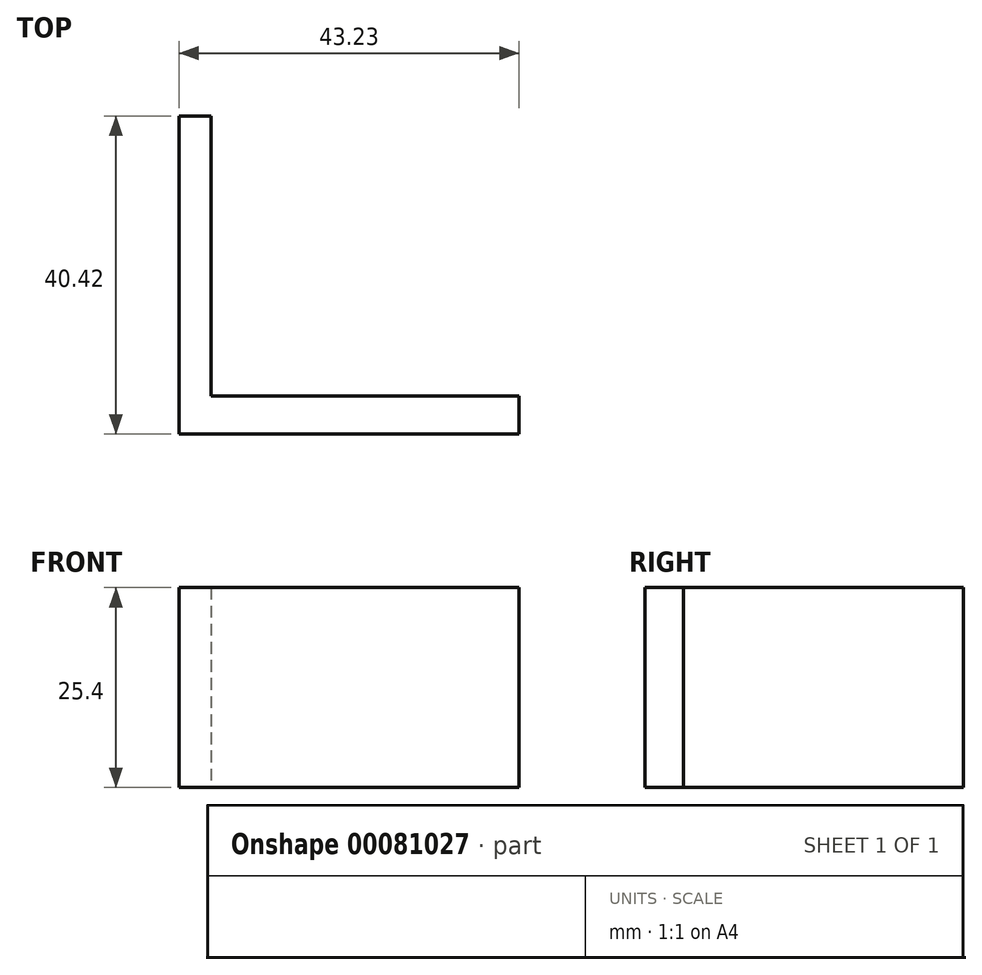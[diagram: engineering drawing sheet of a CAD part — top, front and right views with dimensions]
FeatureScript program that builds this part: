
annotation { "Feature Type Name" : "Feature", "Feature Type Description" : "" }
export const myFeature = defineFeature(function(context is Context, id is Id, definition is map)
    precondition{}
    {
        {
            var Q0;
            Q0=qCreatedBy(makeId("Top.planeOp"),FACE);
            var sketch = newSketch(context, id + "F0", { "sketchPlane" : qUnion([Q0])});
            skLineSegment(sketch, "E0", {"start": v(-22.77, 23.4) * mm, "end": v(-22.77, -17.01) * mm});
            skLineSegment(sketch, "E1", {"start": v(-22.77, -17.01) * mm, "end": v(20.46, -17.01) * mm});
            skLineSegment(sketch, "E2", {"start": v(20.46, -17.01) * mm, "end": v(20.46, -12.15) * mm});
            skLineSegment(sketch, "E3", {"start": v(20.46, -12.15) * mm, "end": v(-18.67, -12.15) * mm});
            skLineSegment(sketch, "E4", {"start": v(-18.67, -12.15) * mm, "end": v(-18.67, 23.4) * mm});
            skLineSegment(sketch, "E5", {"start": v(-18.67, 23.4) * mm, "end": v(-22.77, 23.4) * mm});
            skSolve(sketch);
        }
        {
            var Q0;
            Q0 = qSketchRegion(id + "F0", true);
            extrude(context, id + "F1", {"entities" : qUnion([Q0]), "depth" : 25.4 * mm});
        }
    });
